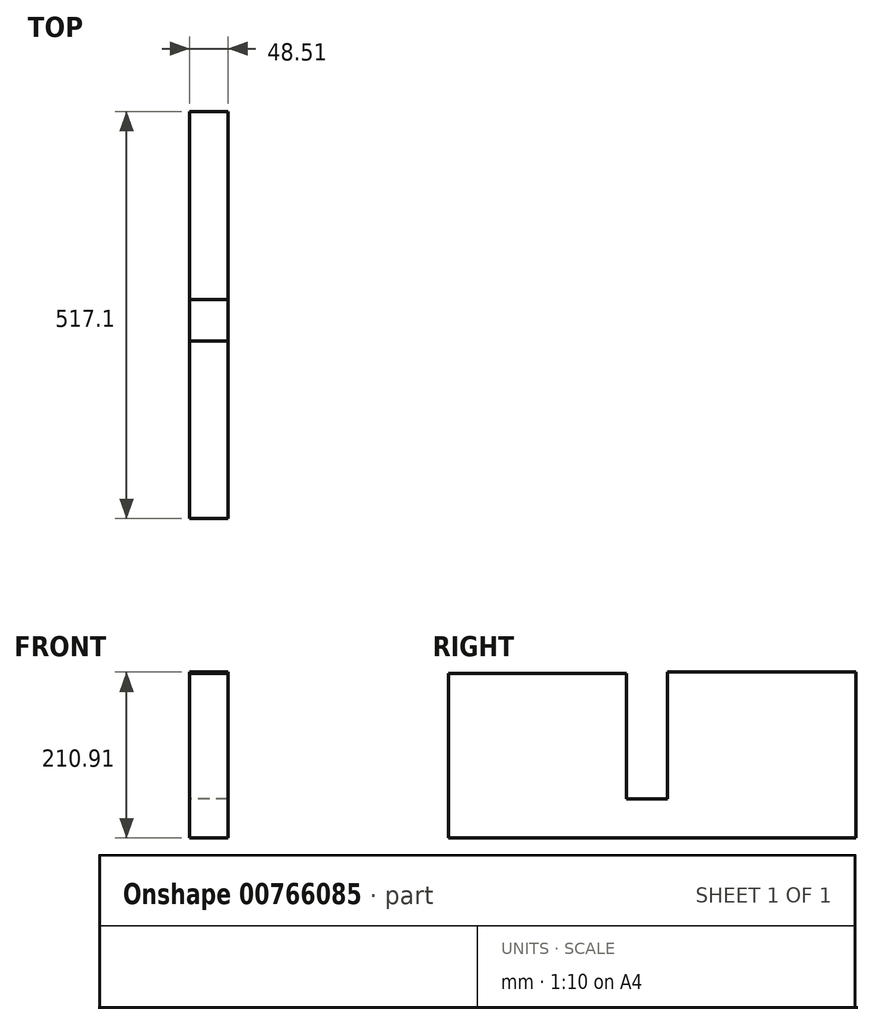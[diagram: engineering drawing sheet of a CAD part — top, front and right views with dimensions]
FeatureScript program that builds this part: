
annotation { "Feature Type Name" : "Feature", "Feature Type Description" : "" }
export const myFeature = defineFeature(function(context is Context, id is Id, definition is map)
    precondition{}
    {
        {
            var Q0;
            Q0=qCreatedBy(makeId("Right.planeOp"),FACE);
            var sketch = newSketch(context, id + "F0", { "sketchPlane" : qUnion([Q0])});
            skLineSegment(sketch, "E0.bottom", {"start": v(-79.7, 49.96) * mm, "end": v(-27.17, 49.96) * mm});
            skLineSegment(sketch, "E0.top", {"start": v(-79.7, 0) * mm, "end": v(-27.17, 0) * mm});
            skLineSegment(sketch, "E0.left", {"start": v(-79.7, 49.96) * mm, "end": v(-79.7, 0) * mm});
            skLineSegment(sketch, "E0.right", {"start": v(-27.17, 49.96) * mm, "end": v(-27.17, 0) * mm});
            skSolve(sketch);
        }
        {
            var Q0;
            Q0=makeQuery(id+"F0.imprint","IMPRINT",FACE,{"disambiguationData":[TD([[makeQuery(id+"F0.imprint","IMPRINT",EDGE,{"derivedFrom":sQuery(id+"F0.wireOp",EDGE,"E0.bottom")}),-1.0]])]});
            extrude(context, id + "F1", {"entities" : qUnion([Q0]), "depth" : 48.5 * mm, "offsetDistance" : 25.4 * mm});
        }
        {
            var Q0;
            Q0=makeQuery(id+"F91kZxVvz0C7wt8_1.boolean.opBoolean","MERGE",FACE,{"derivedFrom":[makeQuery(id+"F1.opExtrude","SWEPT_FACE",FACE,{"disambiguationData":[OSD([sQuery(id+"F0.wireOp",EDGE,"E0.left")])]}),makeQuery(id+"F91kZxVvz0C7wt8_1.opExtrude","SWEPT_FACE",FACE,{"disambiguationData":[OSD([sQuery(id+"Fga7394lB2renw9_1.wireOp",EDGE,"mvRDLbbZ-YgFX-Hhny-qGYf-Rdw3cmQhgzCi.bottom")])]})]});
            var sketch = newSketch(context, id + "F2", { "sketchPlane" : qUnion([Q0])});
            skLineSegment(sketch, "E1.bottom", {"start": v(48.51, 24.98) * mm, "end": v(0, 24.98) * mm});
            skLineSegment(sketch, "E1.top", {"start": v(48.51, 0) * mm, "end": v(0, 0) * mm});
            skLineSegment(sketch, "E1.left", {"start": v(48.51, 24.98) * mm, "end": v(48.51, 0) * mm});
            skLineSegment(sketch, "E1.right", {"start": v(0, 24.98) * mm, "end": v(0, 0) * mm});
            skSolve(sketch);
        }
        {
            var Q0;
            Q0=makeQuery(id+"F2.imprint","IMPRINT",FACE,{"disambiguationData":[TD([[makeQuery(id+"F2.imprint","IMPRINT",EDGE,{"derivedFrom":sQuery(id+"F2.wireOp",EDGE,"E1.bottom")}),1.0]])]});
            extrude(context, id + "F3", {"entities" : qUnion([Q0]), "operationType" : NewBodyOperationType.ADD, "depth" : 47 * mm, "offsetDistance" : 25.4 * mm});
        }
        {
            var Q0;
            Q0=makeQuery(id+"F91kZxVvz0C7wt8_1.boolean.opBoolean","MERGE",FACE,{"derivedFrom":[makeQuery(id+"F1.opExtrude","SWEPT_FACE",FACE,{"disambiguationData":[OSD([sQuery(id+"F0.wireOp",EDGE,"E0.right")])]}),makeQuery(id+"F91kZxVvz0C7wt8_1.opExtrude","SWEPT_FACE",FACE,{"disambiguationData":[OSD([sQuery(id+"Fga7394lB2renw9_1.wireOp",EDGE,"mvRDLbbZ-YgFX-Hhny-qGYf-Rdw3cmQhgzCi.top")])]})]});
            var sketch = newSketch(context, id + "F4", { "sketchPlane" : qUnion([Q0])});
            skLineSegment(sketch, "E2.bottom", {"start": v(-48.51, 0) * mm, "end": v(0, 0) * mm});
            skLineSegment(sketch, "E2.top", {"start": v(-48.51, 24.98) * mm, "end": v(0, 24.98) * mm});
            skLineSegment(sketch, "E2.left", {"start": v(-48.51, 0) * mm, "end": v(-48.51, 24.98) * mm});
            skLineSegment(sketch, "E2.right", {"start": v(0, 0) * mm, "end": v(0, 24.98) * mm});
            skSolve(sketch);
        }
        {
            var Q0;
            Q0=makeQuery(id+"F4.imprint","IMPRINT",FACE,{"disambiguationData":[TD([[makeQuery(id+"F4.imprint","IMPRINT",EDGE,{"derivedFrom":sQuery(id+"F4.wireOp",EDGE,"E2.bottom")}),1.0]])]});
            extrude(context, id + "F5", {"entities" : qUnion([Q0]), "operationType" : NewBodyOperationType.ADD, "depth" : 49.53 * mm, "offsetDistance" : 25.4 * mm});
        }
        {
            var Q0;
            Q0=makeQuery(id+"F5.opExtrude","SWEPT_FACE",FACE,{"disambiguationData":[OSD([sQuery(id+"F4.wireOp",EDGE,"E2.top")])]});
            var sketch = newSketch(context, id + "F6", { "sketchPlane" : qUnion([Q0])});
            skLineSegment(sketch, "E3.bottom", {"start": v(0, 22.36) * mm, "end": v(48.51, 22.36) * mm});
            skLineSegment(sketch, "E3.top", {"start": v(0, -27.17) * mm, "end": v(48.51, -27.17) * mm});
            skLineSegment(sketch, "E3.left", {"start": v(0, 22.36) * mm, "end": v(0, -27.17) * mm});
            skLineSegment(sketch, "E3.right", {"start": v(48.51, 22.36) * mm, "end": v(48.51, -27.17) * mm});
            skSolve(sketch);
        }
        {
            var Q0;
            Q0=makeQuery(id+"F6.imprint","IMPRINT",FACE,{"disambiguationData":[TD([[makeQuery(id+"F6.imprint","IMPRINT",EDGE,{"derivedFrom":sQuery(id+"F6.wireOp",EDGE,"E3.bottom")}),1.0]])]});
            extrude(context, id + "F7", {"entities" : qUnion([Q0]), "operationType" : NewBodyOperationType.ADD, "depth" : 45.72 * mm, "offsetDistance" : 25.4 * mm});
        }
        {
            var Q0;
            Q0=makeQuery(id+"F3.opExtrude","SWEPT_FACE",FACE,{"disambiguationData":[OSD([sQuery(id+"F2.wireOp",EDGE,"E1.bottom")])]});
            var sketch = newSketch(context, id + "F8", { "sketchPlane" : qUnion([Q0])});
            skLineSegment(sketch, "E4.bottom", {"start": v(0, -79.7) * mm, "end": v(48.51, -79.7) * mm});
            skLineSegment(sketch, "E4.top", {"start": v(0, -126.7) * mm, "end": v(48.51, -126.7) * mm});
            skLineSegment(sketch, "E4.left", {"start": v(0, -79.7) * mm, "end": v(0, -126.7) * mm});
            skLineSegment(sketch, "E4.right", {"start": v(48.51, -79.7) * mm, "end": v(48.51, -126.7) * mm});
            skSolve(sketch);
        }
        {
            var Q0;
            Q0=makeQuery(id+"F8.imprint","IMPRINT",FACE,{"disambiguationData":[TD([[makeQuery(id+"F8.imprint","IMPRINT",EDGE,{"derivedFrom":sQuery(id+"F8.wireOp",EDGE,"E4.bottom")}),1.0]])]});
            extrude(context, id + "F9", {"entities" : qUnion([Q0]), "operationType" : NewBodyOperationType.ADD, "depth" : 45.97 * mm, "offsetDistance" : 25.4 * mm});
        }
        {
            var Q0;
            Q0=makeQuery(id+"F9.opExtrude","CAP_FACE",FACE,{"disambiguationData":[OSD([sQuery(id+"F8.wireOp",EDGE,"E4.bottom"),sQuery(id+"F8.wireOp",EDGE,"E4.top"),sQuery(id+"F8.wireOp",EDGE,"E4.left"),sQuery(id+"F8.wireOp",EDGE,"E4.right")])],"isStart":false});
            var sketch = newSketch(context, id + "F10", { "sketchPlane" : qUnion([Q0])});
            skLineSegment(sketch, "E5.bottom", {"start": v(0, -126.7) * mm, "end": v(48.51, -126.7) * mm});
            skLineSegment(sketch, "E5.top", {"start": v(0, -79.7) * mm, "end": v(48.51, -79.7) * mm});
            skLineSegment(sketch, "E5.left", {"start": v(0, -126.7) * mm, "end": v(0, -79.7) * mm});
            skLineSegment(sketch, "E5.right", {"start": v(48.51, -126.7) * mm, "end": v(48.51, -79.7) * mm});
            skLineSegment(sketch, "E6.bottom", {"start": v(0, -25.64) * mm, "end": v(48.51, -25.64) * mm});
            skLineSegment(sketch, "E6.top", {"start": v(0, 23.05) * mm, "end": v(48.51, 23.05) * mm});
            skLineSegment(sketch, "E6.left", {"start": v(0, -25.64) * mm, "end": v(0, 23.05) * mm});
            skLineSegment(sketch, "E6.right", {"start": v(48.51, -25.64) * mm, "end": v(48.51, 23.05) * mm});
            skSolve(sketch);
        }
        {
            var Q0;
            Q0=makeQuery(id+"F10.imprint","IMPRINT",FACE,{"disambiguationData":[TD([[makeQuery(id+"F10.imprint","IMPRINT",EDGE,{"derivedFrom":sQuery(id+"F10.wireOp",EDGE,"E5.bottom")}),-1.0]])]});
            extrude(context, id + "F11", {"entities" : qUnion([Q0]), "operationType" : NewBodyOperationType.ADD, "depth" : 137.92 * mm, "offsetDistance" : 25.4 * mm});
        }
        {
            var Q0;
            Q0=makeQuery(id+"F7.opExtrude","CAP_FACE",FACE,{"disambiguationData":[OSD([sQuery(id+"F6.wireOp",EDGE,"E3.bottom"),sQuery(id+"F6.wireOp",EDGE,"E3.top"),sQuery(id+"F6.wireOp",EDGE,"E3.left"),sQuery(id+"F6.wireOp",EDGE,"E3.right")])],"isStart":false});
            extrude(context, id + "F12", {"entities" : qUnion([Q0]), "operationType" : NewBodyOperationType.ADD, "depth" : 140.2 * mm, "offsetDistance" : 25.4 * mm});
        }
        {
            var Q0;
            Q0=makeQuery(id+"F11.boolean.opBoolean","MERGE",FACE,{"derivedFrom":[makeQuery(id+"F9.boolean.opBoolean","MERGE",FACE,{"derivedFrom":[makeQuery(id+"F3.opExtrude","CAP_FACE",FACE,{"disambiguationData":[OSD([sQuery(id+"F2.wireOp",EDGE,"E1.bottom"),sQuery(id+"F2.wireOp",EDGE,"E1.top"),sQuery(id+"F2.wireOp",EDGE,"E1.left"),sQuery(id+"F2.wireOp",EDGE,"E1.right")])],"isStart":false}),makeQuery(id+"F9.opExtrude","SWEPT_FACE",FACE,{"disambiguationData":[OSD([sQuery(id+"F8.wireOp",EDGE,"E4.top")])]})]}),makeQuery(id+"F11.opExtrude","SWEPT_FACE",FACE,{"disambiguationData":[OSD([sQuery(id+"F10.wireOp",EDGE,"E5.bottom")])]})]});
            var sketch = newSketch(context, id + "F13", { "sketchPlane" : qUnion([Q0])});
            skPoint(sketch, "E7", {"position": v(24.26, 104.44) * mm});
            skPoint(sketch, "E7.positionSnap0", {"position": v(48.51, 104.44) * mm});
            skPoint(sketch, "E7.positionSnap1", {"position": v(24.26, 208.88) * mm});
            skSolve(sketch);
        }
        {
            var Q0;
            Q0=makeQuery(id+"F13.imprint","IMPRINT",FACE,{"disambiguationData":[TD([[makeQuery(id+"F13.imprint","IMPRINT",EDGE,{"derivedFrom":makeQuery(id+"F3.opExtrude","CAP_EDGE",EDGE,{"disambiguationData":[OSD([sQuery(id+"F2.wireOp",EDGE,"E1.top")])],"isStart":false})}),-1.0]])]});
            extrude(context, id + "F14", {"entities" : qUnion([Q0]), "operationType" : NewBodyOperationType.ADD, "depth" : 153.16 * mm, "offsetDistance" : 25.4 * mm});
        }
        {
            var Q0;
            Q0=makeQuery(id+"F14.opExtrude","CAP_FACE",FACE,{"disambiguationData":[OSD([sQuery(id+"F2.wireOp",EDGE,"E1.top"),sQuery(id+"F2.wireOp",EDGE,"E1.left"),sQuery(id+"F2.wireOp",EDGE,"E1.right"),sQuery(id+"F8.wireOp",EDGE,"E4.top"),sQuery(id+"F8.wireOp",EDGE,"E4.left"),sQuery(id+"F8.wireOp",EDGE,"E4.right"),sQuery(id+"F10.wireOp",EDGE,"E5.bottom"),sQuery(id+"F10.wireOp",EDGE,"E5.left"),sQuery(id+"F10.wireOp",EDGE,"E5.right")])],"isStart":false});
            var sketch = newSketch(context, id + "F15", { "sketchPlane" : qUnion([Q0])});
            skLineSegment(sketch, "E8.bottom", {"start": v(48.51, 0) * mm, "end": v(0, 0) * mm});
            skLineSegment(sketch, "E8.top", {"start": v(48.51, 211.46) * mm, "end": v(0, 211.46) * mm});
            skLineSegment(sketch, "E8.left", {"start": v(48.51, 0) * mm, "end": v(48.51, 211.46) * mm});
            skLineSegment(sketch, "E8.right", {"start": v(0, 0) * mm, "end": v(0, 211.46) * mm});
            skSolve(sketch);
        }
        {
            var Q0;
            {var subQ0=sQuery(id+"F15.wireOp",EDGE,"E8.bottom");Q0=makeQuery(id+"F15.imprint","IMPRINT",FACE,{"disambiguationData":[TD([[makeQuery(id+"F15.imprint","IMPRINT",EDGE,{"derivedFrom":subQ0}),-1.0]])]});}
            var Q1;
            {var subQ0=sQuery(id+"F6.wireOp",EDGE,"E3.bottom");Q1=makeQuery(id+"F12.boolean.opBoolean","MERGE",FACE,{"derivedFrom":[makeQuery(id+"F7.boolean.opBoolean","MERGE",FACE,{"derivedFrom":[makeQuery(id+"F5.opExtrude","CAP_FACE",FACE,{"disambiguationData":[OSD([sQuery(id+"F4.wireOp",EDGE,"E2.bottom"),sQuery(id+"F4.wireOp",EDGE,"E2.top"),sQuery(id+"F4.wireOp",EDGE,"E2.left"),sQuery(id+"F4.wireOp",EDGE,"E2.right")])],"isStart":false}),makeQuery(id+"F7.opExtrude","SWEPT_FACE",FACE,{"disambiguationData":[OSD([subQ0])]})]}),makeQuery(id+"F12.opExtrude","SWEPT_FACE",FACE,{"disambiguationData":[OSD([subQ0])]})]});}
            extrude(context, id + "F16", {"entities" : qUnion([Q0, Q1]), "operationType" : NewBodyOperationType.ADD, "depth" : 25.4 * mm, "offsetDistance" : 25.4 * mm});
        }
        {
            var Q0;
            {var subQ0=sQuery(id+"F6.wireOp",EDGE,"E3.bottom");Q0=makeQuery(id+"F12.boolean.opBoolean","MERGE",FACE,{"derivedFrom":[makeQuery(id+"F7.boolean.opBoolean","MERGE",FACE,{"derivedFrom":[makeQuery(id+"F5.opExtrude","CAP_FACE",FACE,{"disambiguationData":[OSD([sQuery(id+"F4.wireOp",EDGE,"E2.bottom"),sQuery(id+"F4.wireOp",EDGE,"E2.top"),sQuery(id+"F4.wireOp",EDGE,"E2.left"),sQuery(id+"F4.wireOp",EDGE,"E2.right")])],"isStart":false}),makeQuery(id+"F7.opExtrude","SWEPT_FACE",FACE,{"disambiguationData":[OSD([subQ0])]})]}),makeQuery(id+"F12.opExtrude","SWEPT_FACE",FACE,{"disambiguationData":[OSD([subQ0])]})]});}
            extrude(context, id + "F17", {"entities" : qUnion([Q0]), "operationType" : NewBodyOperationType.ADD, "depth" : 189.48 * mm, "offsetDistance" : 25.4 * mm});
        }
    });
